# Revit family: WIR-PHOTOCELL
name_source: partatom
category: Communication Devices
units: mm (PartAtom-declared; Revit-internal decimal feet)

## family parameters
Cut with Voids When Loaded = No
Host = Face
Maintain Annotation Orientation = No
OmniClass Number = 23.85.80.11.27
OmniClass Title = Lighting Controls
Part Type = Normal
Room Calculation Point = No
Round Connector Dimension = Use Diameter
Shared = Yes

## types (1)
- WIR-PHOTOCELL
    Assembly Code = D5090
    Base = Metal-Galvanized_Steel
    Certifications = ETL/UL 916 Listed
Title 24 Listed
RoHS compliant
    Default Elevation = 48 "
    Description = The wiSCAPE® Photocell provides On/Off lighting control based on detected light. Designed for outdoor lighting applications that require an external photocell, the wiSCAPE Photocell is a bi-directional wireless RF device that can transmit daytime and nighttime commands to a group or zone of wiSCAPE-enabled luminaires
    Housing Material = Paint - Carbon Black
    Manufacturer = NX Lighting Controls
    Model = WIR-PHOTOCELL Series
    Product Features = • On/Off photocell
• Pre-programmed for out-of-the-box photocell operation
• On/Off lighting circuit control with 0-10V full-range dimming
• Bidirectional wirless RF Mesh communications
• Digital input available for motion sensor or switch control
• Military grade AES-128 communication encryption
• Multi-level grouping and multiple scenarios
• Adjustable minimum and maximum dimming levels
• Commercial-grade metering
• Complete integration with wiSCAPE software
    Type Comments = wiSCAPE® External Fixture Module
    URL = https://www.currentlighting.com
    Warranty = 5-Years Warranty

## geometry (parser evidence)
native form markers: Sweep x2
no freeform markers — native parametric forms only
